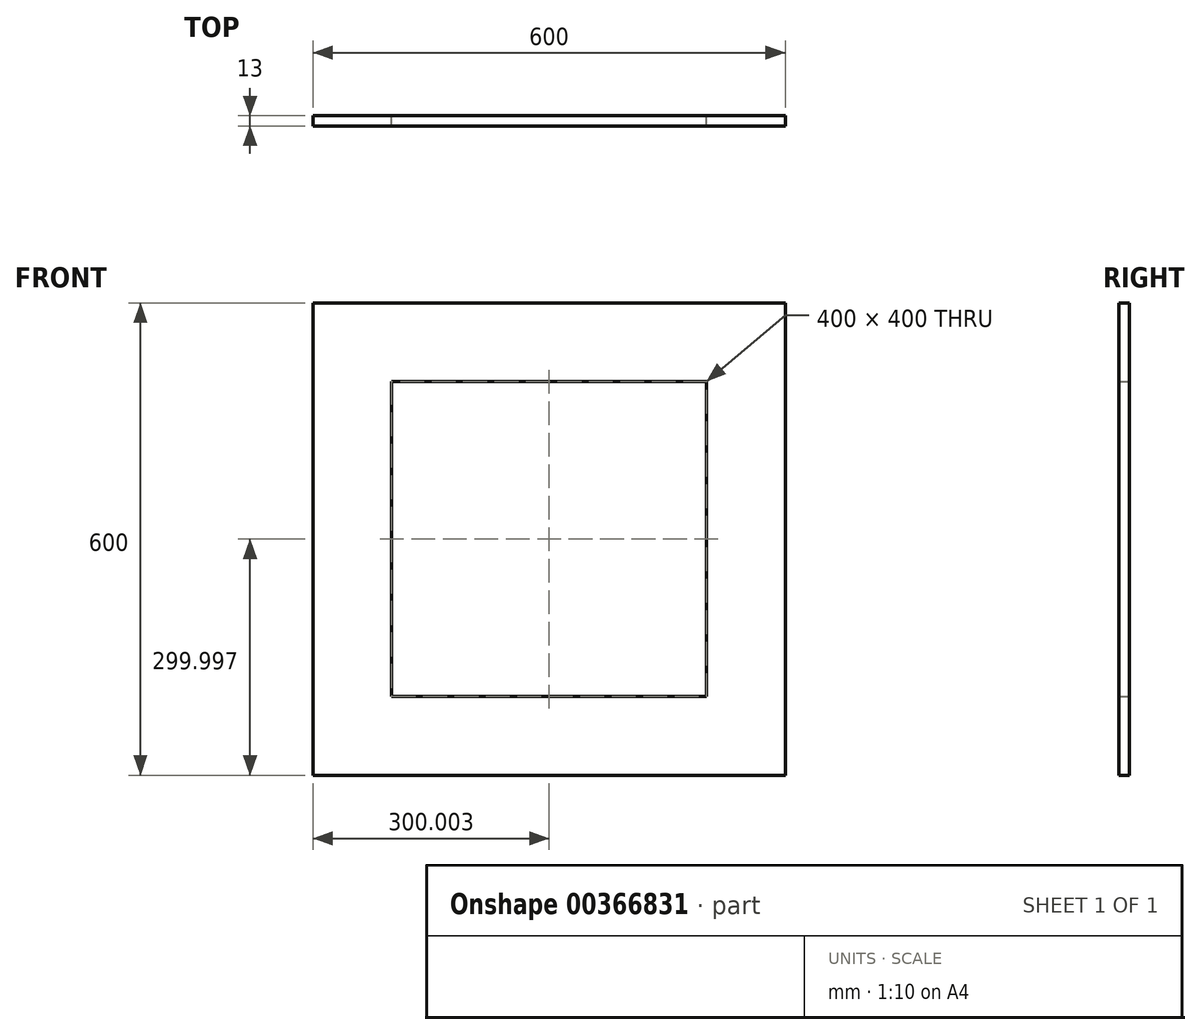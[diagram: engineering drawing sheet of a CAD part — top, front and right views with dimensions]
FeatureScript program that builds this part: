
annotation { "Feature Type Name" : "Feature", "Feature Type Description" : "" }
export const myFeature = defineFeature(function(context is Context, id is Id, definition is map)
    precondition{}
    {
        {
            var Q0;
            Q0=qCreatedBy(makeId("Front.planeOp"),FACE);
            var sketch = newSketch(context, id + "F0", { "sketchPlane" : qUnion([Q0])});
            skLineSegment(sketch, "E0.bottom", {"start": v(-665.94, 566.97) * mm, "end": v(-65.94, 566.97) * mm});
            skLineSegment(sketch, "E0.top", {"start": v(-665.94, -33.03) * mm, "end": v(-65.94, -33.03) * mm});
            skLineSegment(sketch, "E0.left", {"start": v(-665.94, 566.97) * mm, "end": v(-665.94, -33.03) * mm});
            skLineSegment(sketch, "E0.right", {"start": v(-65.94, 566.97) * mm, "end": v(-65.94, -33.03) * mm});
            skSolve(sketch);
        }
        {
            var Q0;
            Q0=makeQuery(id+"F0.imprint","IMPRINT",FACE,{"disambiguationData":[TD([[makeQuery(id+"F0.imprint","IMPRINT",EDGE,{"derivedFrom":sQuery(id+"F0.wireOp",EDGE,"E0.bottom")}),-1.0]])]});
            var sketch = newSketch(context, id + "F1", { "sketchPlane" : qUnion([Q0])});
            skLineSegment(sketch, "E1.bottom", {"start": v(-165.94, 466.97) * mm, "end": v(-565.94, 466.97) * mm});
            skLineSegment(sketch, "E1.top", {"start": v(-165.94, 66.97) * mm, "end": v(-565.94, 66.97) * mm});
            skLineSegment(sketch, "E1.left", {"start": v(-165.94, 466.97) * mm, "end": v(-165.94, 66.97) * mm});
            skLineSegment(sketch, "E1.right", {"start": v(-565.94, 466.97) * mm, "end": v(-565.94, 66.97) * mm});
            skPoint(sketch, "E1.middle", {"position": v(-365.94, 266.97) * mm});
            skSolve(sketch);
        }
        {
            var Q0;
            Q0=makeQuery(id+"F1.imprint","IMPRINT",FACE,{"disambiguationData":[TD([[makeQuery(id+"F1.imprint","IMPRINT",EDGE,{"derivedFrom":sQuery(id+"F1.wireOp",EDGE,"E1.bottom")}),-1.0]])]});
            extrude(context, id + "F2", {"entities" : qUnion([Q0]), "depth" : 13 * mm});
        }
    });
